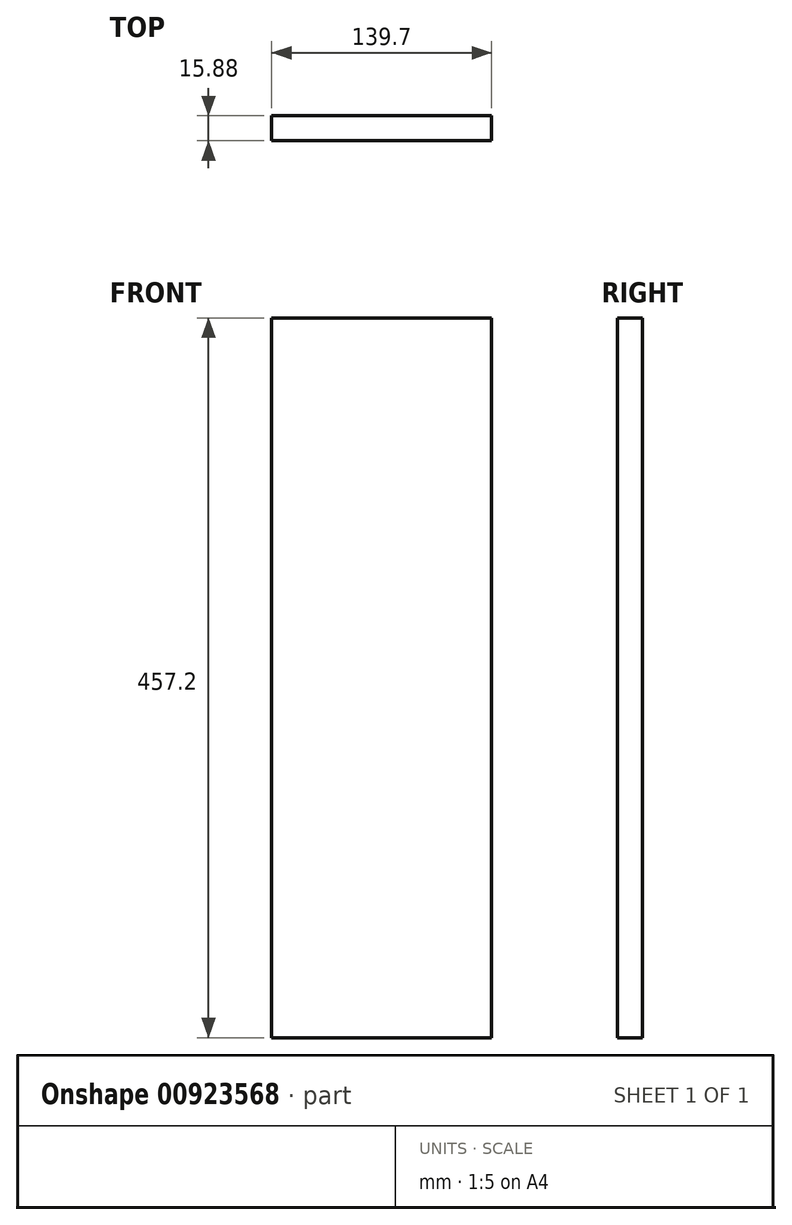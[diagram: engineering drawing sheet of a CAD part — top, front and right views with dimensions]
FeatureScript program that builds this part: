
annotation { "Feature Type Name" : "Feature", "Feature Type Description" : "" }
export const myFeature = defineFeature(function(context is Context, id is Id, definition is map)
    precondition{}
    {
        {
            var Q0;
            Q0=qCreatedBy(makeId("Front.planeOp"),FACE);
            var sketch = newSketch(context, id + "F0", { "sketchPlane" : qUnion([Q0])});
            skLineSegment(sketch, "E0.bottom", {"start": v(0, 0) * mm, "end": v(139.7, 0) * mm});
            skLineSegment(sketch, "E0.top", {"start": v(0, 457.2) * mm, "end": v(139.7, 457.2) * mm});
            skLineSegment(sketch, "E0.left", {"start": v(0, 0) * mm, "end": v(0, 457.2) * mm});
            skLineSegment(sketch, "E0.right", {"start": v(139.7, 0) * mm, "end": v(139.7, 457.2) * mm});
            skSolve(sketch);
        }
        {
            var Q0;
            Q0=makeQuery(id+"F0.imprint","IMPRINT",FACE,{"disambiguationData":[TD([[makeQuery(id+"F0.imprint","IMPRINT",EDGE,{"derivedFrom":sQuery(id+"F0.wireOp",EDGE,"E0.bottom")}),1.0]])]});
            extrude(context, id + "F1", {"entities" : qUnion([Q0]), "depth" : 15.88 * mm, "offsetDistance" : 25.4 * mm});
        }
    });
